# Revit family: NBS_INTRAMattingSystems_EntMatt_INTRAlux-Premier
name_source: partatom
category: Generic Models
revit_build: Autodesk Revit 2013 (Build: 20121003_2115(x64)
units: mm (PartAtom-declared; Revit-internal decimal feet)

## types (1)
- INTRAlux-Premier
    Arrangement = Interior surface mounted.
    AssetType = Fixed
    BIMObjectName = NBS_INTRAMattingSystems_EntranceMatting_INTRAlux-Premier
    Combustible = Yes
    Constituents = High content PVC backing with polyamide pile and nylon monofilaments.
    Default Elevation = 0 mm  [stored 0 ft]
    Description = High quality polyamide sheet fibre barrier matting.
    DurationUnit = year
    EntranceMattingMaterial = NBS_INTRAMattingSystems_EntranceMatting_INTRAlux-Premier
    ExpectedLife = 3-5 years
    FireRating = Cfl-s1
    HasAntiStaticSurface = No
    HasNonSkidSurface = Yes
    IfcExportAs = IfcCoveringType
    IfcExportType = FLOORING
    InsertColourOptions = 007 Anthracite or 014 Grey.
    ManufacturerName = INTRAmatting Systems
    ManufacturerURL = www.intramatting.com
    MattingHeight = 9mm
    ModelReference = INTRAlux Premier
    NBSCertification = www.nationalbimlibrary.com/intramatting-systems/intralux-premier
    NBSDescription = Entrance matting
    NBSReference = 45-35-35/420
    Name = EntranceMatting_INTRAlux-Premier
    NominalHeight = 9 mm  [stored 0.0295276 ft]
    NominalLength = 0 mm  [stored 0 ft]
    NominalWidth = 0 mm  [stored 0 ft]
    ProductInformation = www.intramatting.com/product_download.php
    Shape = To be installed to any matwell shape/size
    Size = Roll: 2000mm x 25m.
    Thickness = 9 mm  [stored 0.0295276 ft]
    TotalThickness = 9 mm  [stored 0.0295276 ft]
    Uniclass2 = 45-57-11/426
    Version = 1
    Weight = 3360g/m²

note: [stored X ft] marks values corroborated as IEEE doubles in the binary element streams (Revit-internal decimal feet)

## geometry (parser evidence)
native form markers: Sweep x1
no freeform markers — native parametric forms only
